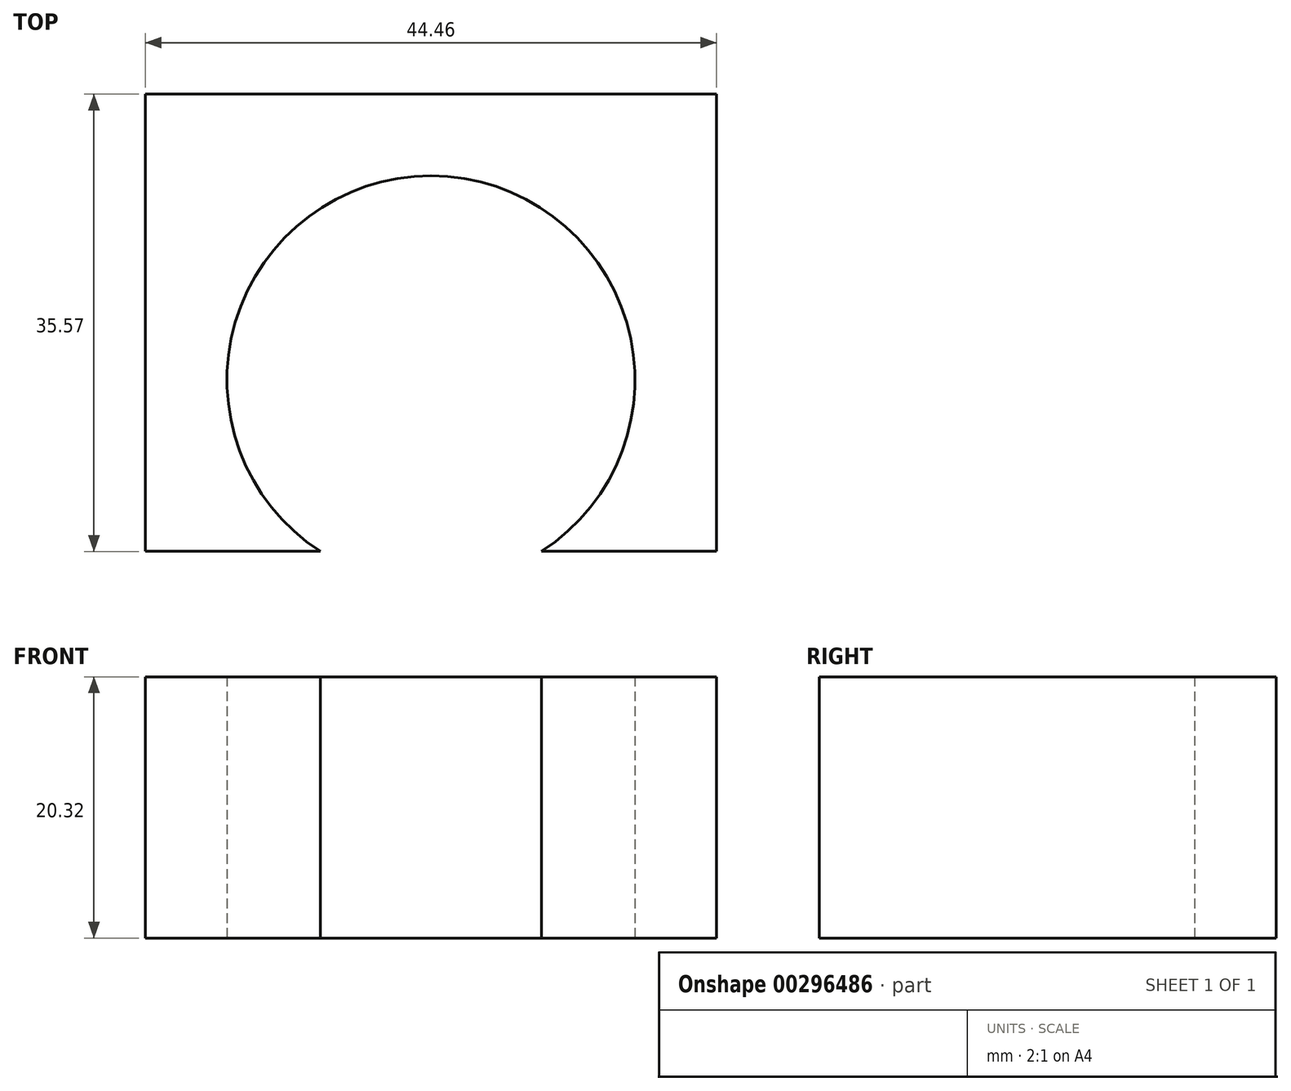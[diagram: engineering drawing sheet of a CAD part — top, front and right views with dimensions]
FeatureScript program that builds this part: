
annotation { "Feature Type Name" : "Feature", "Feature Type Description" : "" }
export const myFeature = defineFeature(function(context is Context, id is Id, definition is map)
    precondition{}
    {
        {
            var Q0;
            Q0=qCreatedBy(makeId("Top.planeOp"),FACE);
            var sketch = newSketch(context, id + "F0", { "sketchPlane" : qUnion([Q0])});
            skCircle(sketch, "E0", {"center": v(0, 0) * mm, "radius": 15.88 * mm});
            skLineSegment(sketch, "E1.bottom", {"start": v(-22.23, 22.23) * mm, "end": v(22.23, 22.23) * mm});
            skLineSegment(sketch, "E1.top", {"start": v(-22.23, -22.23) * mm, "end": v(22.23, -22.23) * mm});
            skLineSegment(sketch, "E1.left", {"start": v(-22.23, 22.23) * mm, "end": v(-22.23, -22.23) * mm});
            skLineSegment(sketch, "E1.right", {"start": v(22.23, 22.23) * mm, "end": v(22.23, -22.23) * mm});
            skSolve(sketch);
        }
        {
            var Q0;
            Q0=makeQuery(id+"F0.imprint","IMPRINT",FACE,{"disambiguationData":[TD([[makeQuery(id+"F0.imprint","IMPRINT",EDGE,{"derivedFrom":sQuery(id+"F0.wireOp",EDGE,"E0")}),-1.0]])]});
            extrude(context, id + "F1", {"entities" : qUnion([Q0]), "depth" : 20.32 * mm});
        }
        {
            var Q0;
            Q0=makeQuery(id+"F1.opExtrude","CAP_FACE",FACE,{"disambiguationData":[OSD([sQuery(id+"F0.wireOp",EDGE,"E0"),sQuery(id+"F0.wireOp",EDGE,"E1.bottom"),sQuery(id+"F0.wireOp",EDGE,"E1.top"),sQuery(id+"F0.wireOp",EDGE,"E1.left"),sQuery(id+"F0.wireOp",EDGE,"E1.right")])],"isStart":false});
            var sketch = newSketch(context, id + "F2", { "sketchPlane" : qUnion([Q0])});
            skLineSegment(sketch, "E2.bottom", {"start": v(-22.23, -22.23) * mm, "end": v(22.23, -22.23) * mm});
            skLineSegment(sketch, "E2.top", {"start": v(-22.23, -13.34) * mm, "end": v(22.23, -13.34) * mm});
            skLineSegment(sketch, "E2.left", {"start": v(-22.23, -22.23) * mm, "end": v(-22.23, -13.34) * mm});
            skLineSegment(sketch, "E2.right", {"start": v(22.23, -22.23) * mm, "end": v(22.23, -13.34) * mm});
            skSolve(sketch);
        }
        {
            var Q0;
            Q0=makeQuery(id+"F2.imprint","IMPRINT",FACE,{"disambiguationData":[TD([[makeQuery(id+"F2.imprint","IMPRINT",EDGE,{"derivedFrom":sQuery(id+"F2.wireOp",EDGE,"E2.bottom")}),1.0]])]});
            extrude(context, id + "F3", {"entities" : qUnion([Q0]), "operationType" : NewBodyOperationType.REMOVE, "endBound" : BoundingType.THROUGH_ALL, "oppositeDirection" : true, "depth" : 25.4 * mm});
        }
    });
